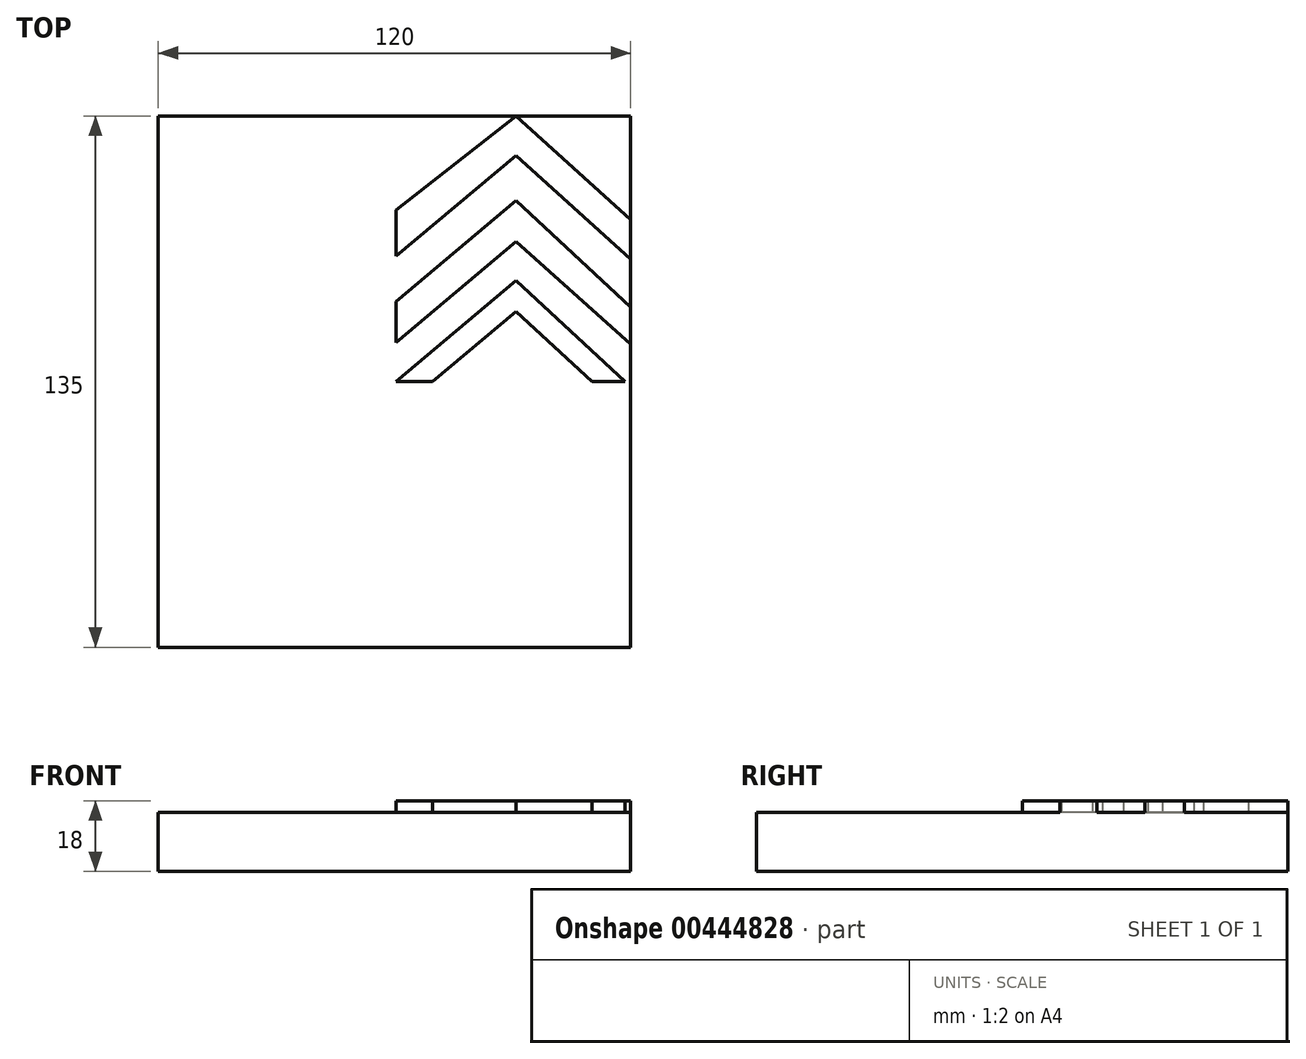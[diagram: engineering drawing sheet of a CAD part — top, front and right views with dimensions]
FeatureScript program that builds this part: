
annotation { "Feature Type Name" : "Feature", "Feature Type Description" : "" }
export const myFeature = defineFeature(function(context is Context, id is Id, definition is map)
    precondition{}
    {
        {
            var Q0;
            Q0=qCreatedBy(makeId("Top.planeOp"),FACE);
            var sketch = newSketch(context, id + "F0", { "sketchPlane" : qUnion([Q0])});
            skLineSegment(sketch, "E0.bottom", {"start": v(-60, 67.5) * mm, "end": v(60, 67.5) * mm});
            skLineSegment(sketch, "E0.top", {"start": v(-60, -67.5) * mm, "end": v(60, -67.5) * mm});
            skLineSegment(sketch, "E0.left", {"start": v(-60, 67.5) * mm, "end": v(-60, -67.5) * mm});
            skLineSegment(sketch, "E0.right", {"start": v(60, 67.5) * mm, "end": v(60, -67.5) * mm});
            skLineSegment(sketch, "E1", {"start": v(0, 67.5) * mm, "end": v(0, -67.5) * mm});
            skLineSegment(sketch, "E2", {"start": v(-60, 0) * mm, "end": v(60, 0) * mm});
            skLineSegment(sketch, "E3", {"start": v(5.98, 0) * mm, "end": v(29.66, 16.67) * mm});
            skSolve(sketch);
        }
        {
            var Q0;
            Q0 = qSketchRegion(id + "F0", true);
            extrude(context, id + "F1", {"entities" : qUnion([Q0]), "depth" : 15 * mm});
        }
        {
            var Q0;
            Q0=makeQuery(id+"F1.opExtrude","CAP_FACE",FACE,{"disambiguationData":[OSD([sQuery(id+"F0.wireOp",EDGE,"E0.bottom"),sQuery(id+"F0.wireOp",EDGE,"E0.top"),sQuery(id+"F0.wireOp",EDGE,"E0.left"),sQuery(id+"F0.wireOp",EDGE,"E0.right")])],"isStart":false});
            var sketch = newSketch(context, id + "F2", { "sketchPlane" : qUnion([Q0])});
            skLineSegment(sketch, "E4", {"start": v(30.81, 17.82) * mm, "end": v(9.66, 0) * mm});
            skLineSegment(sketch, "E5", {"start": v(30.81, 17.82) * mm, "end": v(50.12, 0) * mm});
            skLineSegment(sketch, "E6", {"start": v(30.81, 25.64) * mm, "end": v(58.6, 0) * mm});
            skLineSegment(sketch, "E7", {"start": v(30.81, 25.64) * mm, "end": v(0.38, 0) * mm});
            skLineSegment(sketch, "E8", {"start": v(0, 0) * mm, "end": v(60, 0) * mm});
            skLineSegment(sketch, "E9", {"start": v(0.38, 67.5) * mm, "end": v(0.38, 0) * mm});
            skLineSegment(sketch, "E10", {"start": v(30.81, 35.52) * mm, "end": v(0, 9.57) * mm});
            skLineSegment(sketch, "E11", {"start": v(30.81, 35.52) * mm, "end": v(60, 9.57) * mm});
            skLineSegment(sketch, "E12", {"start": v(0.38, 20.35) * mm, "end": v(30.81, 45.99) * mm});
            skLineSegment(sketch, "E13", {"start": v(30.81, 45.99) * mm, "end": v(60, 18.97) * mm});
            skLineSegment(sketch, "E14", {"start": v(0.38, 31.84) * mm, "end": v(30.81, 57.48) * mm});
            skLineSegment(sketch, "E15", {"start": v(30.81, 57.48) * mm, "end": v(60, 31.16) * mm});
            skLineSegment(sketch, "E16", {"start": v(0.38, 43.57) * mm, "end": v(30.81, 67.5) * mm});
            skLineSegment(sketch, "E17", {"start": v(30.81, 67.5) * mm, "end": v(60, 41.17) * mm});
            skSolve(sketch);
        }
        {
            var Q0;
            {var subQ3=sQuery(id+"F2.wireOp",EDGE,"E4");Q0=makeQuery(id+"F2.imprint","IMPRINT",FACE,{"disambiguationData":[TD([[makeQuery(id+"F2.imprint","IMPRINT",EDGE,{"derivedFrom":subQ3}),-1.0]])]});}
            var Q1;
            {var subQ1=sQuery(id+"F2.wireOp",EDGE,"E11");Q1=makeQuery(id+"F2.imprint","IMPRINT",FACE,{"disambiguationData":[TD([[makeQuery(id+"F2.imprint","IMPRINT",EDGE,{"derivedFrom":subQ1}),1.0]])]});}
            var Q2;
            {var subQ1=sQuery(id+"F2.wireOp",EDGE,"E14");Q2=makeQuery(id+"F2.imprint","IMPRINT",FACE,{"disambiguationData":[TD([[makeQuery(id+"F2.imprint","IMPRINT",EDGE,{"derivedFrom":subQ1}),1.0]])]});}
            extrude(context, id + "F3", {"entities" : qUnion([Q0, Q1, Q2]), "operationType" : NewBodyOperationType.ADD, "depth" : 3 * mm});
        }
    });
